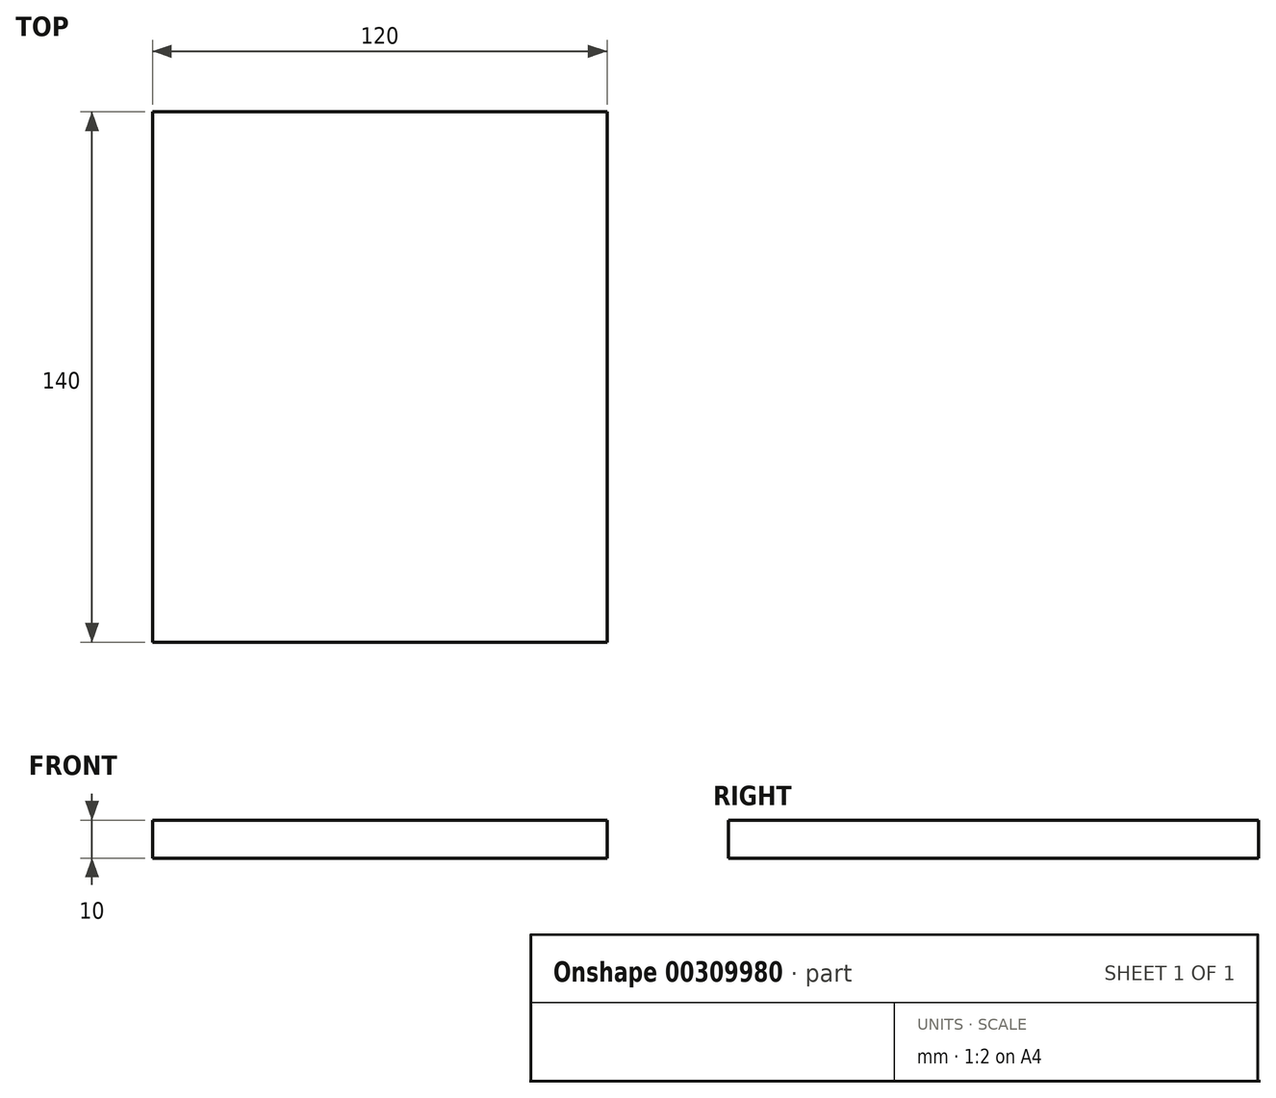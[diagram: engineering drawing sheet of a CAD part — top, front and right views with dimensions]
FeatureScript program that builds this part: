
annotation { "Feature Type Name" : "Feature", "Feature Type Description" : "" }
export const myFeature = defineFeature(function(context is Context, id is Id, definition is map)
    precondition{}
    {
        {
            var Q0;
            Q0=qCreatedBy(makeId("Front.planeOp"),FACE);
            var sketch = newSketch(context, id + "F0", { "sketchPlane" : qUnion([Q0])});
            skLineSegment(sketch, "E0.bottom", {"start": v(-60, 5) * mm, "end": v(60, 5) * mm});
            skLineSegment(sketch, "E0.top", {"start": v(-60, -5) * mm, "end": v(60, -5) * mm});
            skLineSegment(sketch, "E0.left", {"start": v(-60, 5) * mm, "end": v(-60, -5) * mm});
            skLineSegment(sketch, "E0.right", {"start": v(60, 5) * mm, "end": v(60, -5) * mm});
            skPoint(sketch, "E0.middle", {"position": v(0, 0) * mm});
            skSolve(sketch);
        }
        {
            var Q0;
            Q0 = qSketchRegion(id + "F0", true);
            extrude(context, id + "F1", {"entities" : qUnion([Q0]), "depth" : 140 * mm});
        }
    });
